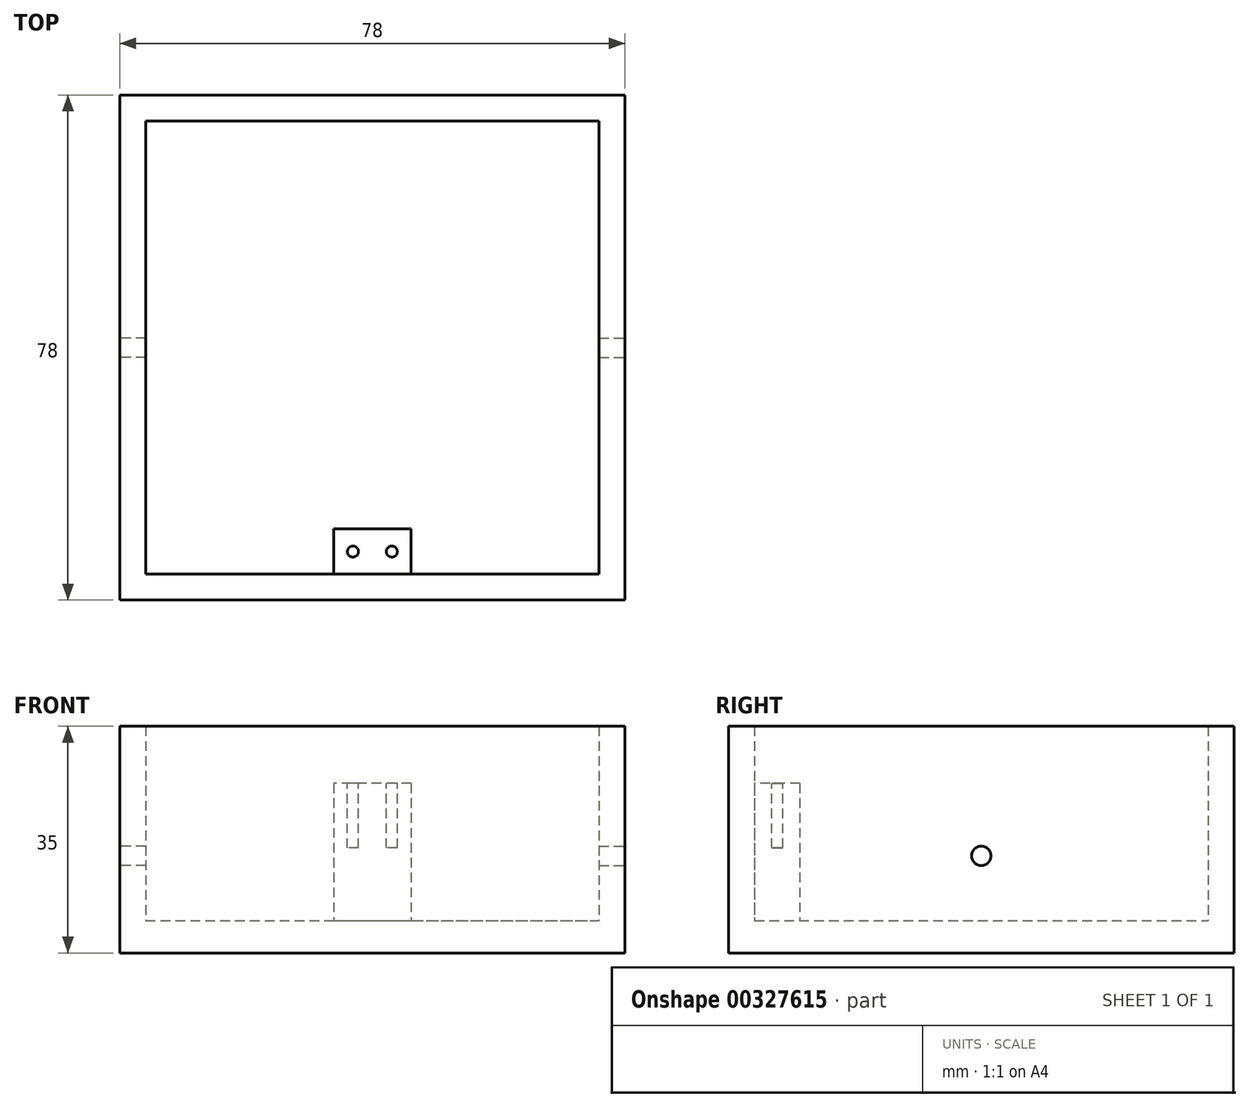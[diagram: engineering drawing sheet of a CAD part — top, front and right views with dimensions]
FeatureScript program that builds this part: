
annotation { "Feature Type Name" : "Feature", "Feature Type Description" : "" }
export const myFeature = defineFeature(function(context is Context, id is Id, definition is map)
    precondition{}
    {
        {
            var Q0;
            Q0=qCreatedBy(makeId("Top.planeOp"),FACE);
            var sketch = newSketch(context, id + "F0", { "sketchPlane" : qUnion([Q0])});
            skLineSegment(sketch, "E0.bottom", {"start": v(0, 0) * mm, "end": v(70, 0) * mm});
            skLineSegment(sketch, "E0.top", {"start": v(0, 70) * mm, "end": v(70, 70) * mm});
            skLineSegment(sketch, "E0.left", {"start": v(0, 0) * mm, "end": v(0, 70) * mm});
            skLineSegment(sketch, "E0.right", {"start": v(70, 0) * mm, "end": v(70, 70) * mm});
            skLineSegment(sketch, "E1.bottom", {"start": v(-4, 74) * mm, "end": v(74, 74) * mm});
            skLineSegment(sketch, "E1.top", {"start": v(-4, -4) * mm, "end": v(74, -4) * mm});
            skLineSegment(sketch, "E1.left", {"start": v(-4, 74) * mm, "end": v(-4, -4) * mm});
            skLineSegment(sketch, "E1.right", {"start": v(74, 74) * mm, "end": v(74, -4) * mm});
            skSolve(sketch);
        }
        {
            var Q0;
            Q0 = qSketchRegion(id + "F0", true);
            extrude(context, id + "F1", {"entities" : qUnion([Q0]), "depth" : 35 * mm});
        }
        {
            var Q0;
            Q0=qCreatedBy(makeId("Top.planeOp"),FACE);
            var sketch = newSketch(context, id + "F2", { "sketchPlane" : qUnion([Q0])});
            skLineSegment(sketch, "E2.bottom", {"start": v(0, 0) * mm, "end": v(70, 0) * mm});
            skLineSegment(sketch, "E2.top", {"start": v(0, 70) * mm, "end": v(70, 70) * mm});
            skLineSegment(sketch, "E2.left", {"start": v(0, 0) * mm, "end": v(0, 70) * mm});
            skLineSegment(sketch, "E2.right", {"start": v(70, 0) * mm, "end": v(70, 70) * mm});
            skSolve(sketch);
        }
        {
            var Q0;
            Q0 = qSketchRegion(id + "F2", true);
            extrude(context, id + "F3", {"entities" : qUnion([Q0]), "operationType" : NewBodyOperationType.ADD, "depth" : 5 * mm});
        }
        {
            var Q0;
            Q0=qCreatedBy(makeId("Top.planeOp"),FACE);
            var sketch = newSketch(context, id + "F4", { "sketchPlane" : qUnion([Q0])});
            skLineSegment(sketch, "E3.bottom", {"start": v(41, 7) * mm, "end": v(29, 7) * mm});
            skLineSegment(sketch, "E3.top", {"start": v(41, 0) * mm, "end": v(29, 0) * mm});
            skLineSegment(sketch, "E3.left", {"start": v(41, 7) * mm, "end": v(41, 0) * mm});
            skLineSegment(sketch, "E3.right", {"start": v(29, 7) * mm, "end": v(29, 0) * mm});
            skSolve(sketch);
        }
        {
            var Q0;
            Q0 = qSketchRegion(id + "F4", true);
            extrude(context, id + "F5", {"entities" : qUnion([Q0]), "operationType" : NewBodyOperationType.ADD, "depth" : 26.2 * mm});
        }
        {
            var Q0;
            Q0=makeQuery(id+"F5.opExtrude","CAP_FACE",FACE,{"disambiguationData":[OSD([sQuery(id+"F4.wireOp",EDGE,"E3.bottom"),sQuery(id+"F4.wireOp",EDGE,"E3.top"),sQuery(id+"F4.wireOp",EDGE,"E3.left"),sQuery(id+"F4.wireOp",EDGE,"E3.right")])],"isStart":false});
            cPlane(context, id + "F6", {"entities" : qUnion([Q0]), "cplaneType" : CPlaneType.OFFSET, "offset" : 0 * mm, "width" : 152.4 * mm, "height" : 152.4 * mm});
        }
        {
            var Q0;
            Q0=qCreatedBy(id+"F6.planeOp",FACE);
            var sketch = newSketch(context, id + "F7", { "sketchPlane" : qUnion([Q0])});
            skCircle(sketch, "E4", {"center": v(38, 3.5) * mm, "radius": 0.85 * mm});
            skCircle(sketch, "E5", {"center": v(32, 3.5) * mm, "radius": 0.85 * mm});
            skSolve(sketch);
        }
        {
            var Q0;
            Q0 = qSketchRegion(id + "F7", true);
            extrude(context, id + "F8", {"entities" : qUnion([Q0]), "operationType" : NewBodyOperationType.REMOVE, "oppositeDirection" : true, "depth" : 10 * mm});
        }
        {
            var Q0;
            Q0=makeQuery(id+"F1.opExtrude","SWEPT_FACE",FACE,{"disambiguationData":[OSD([sQuery(id+"F0.wireOp",EDGE,"E1.right")])]});
            cPlane(context, id + "F9", {"entities" : qUnion([Q0]), "cplaneType" : CPlaneType.OFFSET, "offset" : 0 * mm, "width" : 152.4 * mm, "height" : 152.4 * mm});
        }
        {
            var Q0;
            Q0=qCreatedBy(id+"F9.planeOp",FACE);
            var sketch = newSketch(context, id + "F10", { "sketchPlane" : qUnion([Q0])});
            skCircle(sketch, "E6", {"center": v(35, 15) * mm, "radius": 1.5 * mm});
            skSolve(sketch);
        }
        {
            var Q0;
            Q0 = qSketchRegion(id + "F10", true);
            extrude(context, id + "F11", {"entities" : qUnion([Q0]), "operationType" : NewBodyOperationType.REMOVE, "oppositeDirection" : true, "depth" : 25.4 * mm});
        }
        {
            var Q0;
            Q0=makeQuery(id+"F1.opExtrude","SWEPT_FACE",FACE,{"disambiguationData":[OSD([sQuery(id+"F0.wireOp",EDGE,"E1.left")])]});
            cPlane(context, id + "F12", {"entities" : qUnion([Q0]), "cplaneType" : CPlaneType.OFFSET, "offset" : 0 * mm, "width" : 152.4 * mm, "height" : 152.4 * mm});
        }
        {
            var Q0;
            Q0=qCreatedBy(id+"F12.planeOp",FACE);
            var sketch = newSketch(context, id + "F13", { "sketchPlane" : qUnion([Q0])});
            skCircle(sketch, "E7", {"center": v(-35, 15) * mm, "radius": 1.5 * mm});
            skSolve(sketch);
        }
        {
            var Q0;
            Q0 = qSketchRegion(id + "F13", true);
            extrude(context, id + "F14", {"entities" : qUnion([Q0]), "operationType" : NewBodyOperationType.REMOVE, "oppositeDirection" : true, "depth" : 25.4 * mm});
        }
    });
